# Revit family: NBS_Allermuir_OffcChrs-en-us-Folk_SideChair
name_source: partatom
category: Furniture
revit_build: Autodesk Revit 2018 (Build: 20190510_1515(x64)
units: mm (PartAtom-declared; Revit-internal decimal feet)

## family parameters
Always vertical = Yes
Cut with Voids When Loaded = No
Room Calculation Point = No
Shared = No
Work Plane-Based = No

## types (2) — shared parameters
AssetType = Movable
Category = Pr_40_50_12_57:Office chairs
CodePerformance = BS EN 16139 Level 1
Color = Off black, white, crayon Gray, pistachio, seattle green, aubergine
DurationUnit = year
ExpectedLife = 10
Features = Plastic glides, stacks up to 4 high, two-tone upholstery
Finish = Clear beech, clear oak
FrameFinish = Off black, White, Crayon Gray, Pistachio, Seattle green, Aubergine
FrameMaterial = NBS_Allermuir_Aluminium_BlackPowderCoat
IfcExportAs = IfcFurnitureType
IfcExportType = CHAIR
IsBuiltIn = No
LegMaterial = NBS_Allermuir_Beech_ClearFinish
ManufacturerName = Allermuir
ManufacturerURL = www.allermuir.com
ModelReference = Folk_SideChair
NBSCertification = www.nationalbimlibrary.com/cert/vqm014gw
NBSDescription = Office chairs
NBSReference = 45-35-20/330
NominalDepth = 20 "
NominalHeight = 31 "
NominalLength = 19 "
NominalWidth = 19 "
OmniClassCode = 22-12 52 23
OmniClassTitle = Office Seating
OmniClassVersion = Table 22 2012-05-16
ProductInformation = https://www.allermuir.com
SeatDepth = 17.25"
SeatWidth = 18"
SeatingHeight = 18 "
Status = UNSET
Style = Chair
SustainabilityPerformance = 99% recyclable
Uniclass2015Code = Pr_40_50_12_57
Uniclass2015Title = Office chairs
Uniclass2015Version = Products v1.15
Version = 1
WarrantyDescription = Allermuir warrant that its manufactured products are free from manufacturing defects - in materials or workmanship - for a period of ten (10) years. , Allermuir will repair, or replace (at Allermuir's sole discretion) with comparable free of charge materials / components, any product / component which fails under normal use in a single shift environment, as a result of a defect in the materials and/ or workmanship
WarrantyDurationParts = 10
WarrantyDurationUnit = year
WoodStains = Clear Oak, American Cherry, American Walnut, Dark Walnut, Wenge
zero-valued in all types: HighestSeatingHeight, LowestSeatingHeight

## per-type parameters (varying)
| type | BIMObjectName | Description | Material | ModelNumber | Name | SeatMaterial | Size |
| Folk_SideChair_FLK101 | NBS_Allermuir_OfficeChairs_Folk_SideChair_FLK101-US | Wood seat and back chair | Oak, Aluminum | FLK101 | OfficeChairs_FLK101_Folk_Allermuir | NBS_Allermuir_Beech_ClearFinish | 20 x 31 x 18.75" |
| Folk_SideChair_FLK103 | NBS_Allermuir_OfficeChairs_Folk_SideChair_FLK103-US | Plastic seat and back chair | Plastic, Aluminum | FLK103 | OfficeChairs_FLK103_Folk_Allermuir | NBS_Allermuir_Plastic_Black | 20.5 x 43.25 x 19" |

## geometry (parser evidence)
native form markers: Sweep x6
no freeform markers — native parametric forms only
